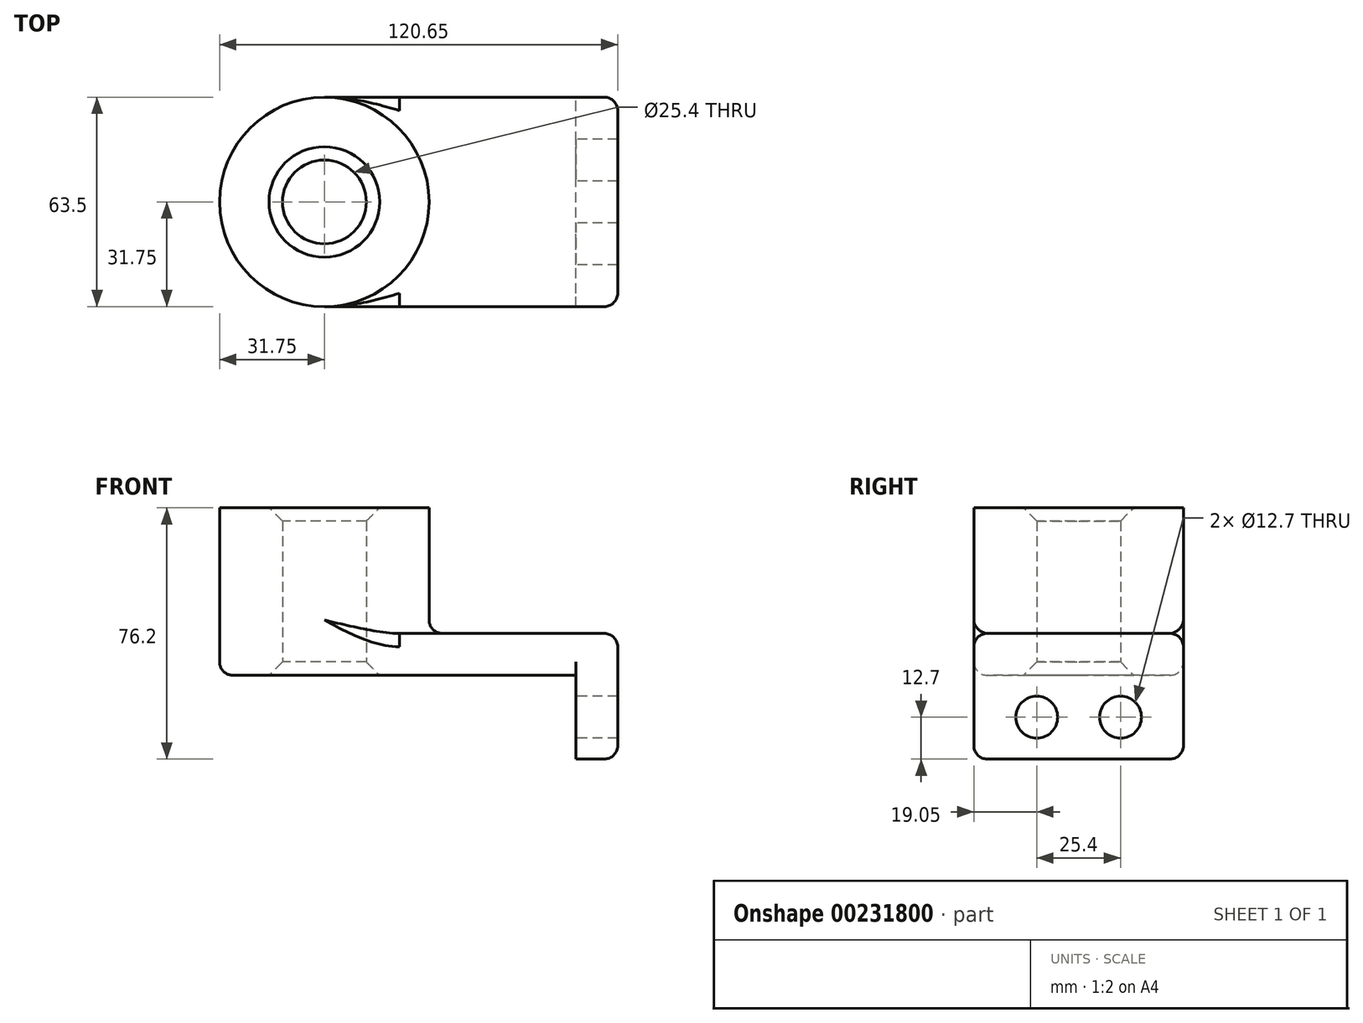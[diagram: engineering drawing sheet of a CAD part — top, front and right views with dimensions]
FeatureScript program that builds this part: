
annotation { "Feature Type Name" : "Feature", "Feature Type Description" : "" }
export const myFeature = defineFeature(function(context is Context, id is Id, definition is map)
    precondition{}
    {
        {
            var Q0;
            Q0=qCreatedBy(makeId("Top.planeOp"),FACE);
            var sketch = newSketch(context, id + "F0", { "sketchPlane" : qUnion([Q0])});
            skLineSegment(sketch, "E0.bottom", {"start": v(-38.1, -31.75) * mm, "end": v(38.1, -31.75) * mm});
            skLineSegment(sketch, "E0.top", {"start": v(-38.1, 31.75) * mm, "end": v(38.1, 31.75) * mm});
            skLineSegment(sketch, "E0.left", {"start": v(-38.1, -31.75) * mm, "end": v(-38.1, 31.75) * mm});
            skLineSegment(sketch, "E0.right", {"start": v(38.1, -31.75) * mm, "end": v(38.1, 31.75) * mm});
            skPoint(sketch, "E0.middle", {"position": v(0, 0) * mm});
            skCircle(sketch, "E1", {"center": v(-38.1, 0) * mm, "radius": 31.75 * mm});
            skCircle(sketch, "E2", {"center": v(-38.1, 0) * mm, "radius": 12.7 * mm});
            skSolve(sketch);
        }
        {
            var Q0;
            Q0 = qSketchRegion(id + "F0", true);
            extrude(context, id + "F1", {"entities" : qUnion([Q0]), "depth" : 12.7 * mm});
        }
        {
            var Q0;
            {var subQ1=sQuery(id+"F0.wireOp",EDGE,"E0.left");var subQ3=sQuery(id+"F0.wireOp",EDGE,"E2");var subQ4=makeQuery(id+"F0.imprint","INTERSECT",VERTEX,{"disambiguationData":[OD(0.0)],"derivedFrom":[subQ1,subQ3]});Q0=makeQuery(id+"F0.imprint","IMPRINT",FACE,{"disambiguationData":[TD([[makeQuery(id+"F0.imprint","IMPRINT",EDGE,{"disambiguationData":[TD([[subQ4,1.0]])],"derivedFrom":subQ3}),-1.0]])]});}
            var Q1;
            {var subQ1=sQuery(id+"F0.wireOp",EDGE,"E0.left");var subQ3=sQuery(id+"F0.wireOp",EDGE,"E2");var subQ4=makeQuery(id+"F0.imprint","INTERSECT",VERTEX,{"disambiguationData":[OD(0.0)],"derivedFrom":[subQ1,subQ3]});Q1=makeQuery(id+"F0.imprint","IMPRINT",FACE,{"disambiguationData":[TD([[makeQuery(id+"F0.imprint","IMPRINT",EDGE,{"disambiguationData":[TD([[subQ4,-1.0]])],"derivedFrom":subQ3}),-1.0]])]});}
            extrude(context, id + "F2", {"entities" : qUnion([Q0, Q1]), "operationType" : NewBodyOperationType.ADD, "depth" : 50.8 * mm});
        }
        {
            var Q0;
            Q0=makeQuery(id+"F1.opExtrude","SWEPT_FACE",FACE,{"disambiguationData":[OSD([sQuery(id+"F0.wireOp",EDGE,"E0.right")])]});
            var sketch = newSketch(context, id + "F3", { "sketchPlane" : qUnion([Q0])});
            skLineSegment(sketch, "E3.bottom", {"start": v(-31.75, 12.7) * mm, "end": v(31.75, 12.7) * mm});
            skLineSegment(sketch, "E3.top", {"start": v(-31.75, -25.4) * mm, "end": v(31.75, -25.4) * mm});
            skLineSegment(sketch, "E3.left", {"start": v(-31.75, 12.7) * mm, "end": v(-31.75, -25.4) * mm});
            skLineSegment(sketch, "E3.right", {"start": v(31.75, 12.7) * mm, "end": v(31.75, -25.4) * mm});
            skCircle(sketch, "E4", {"center": v(-12.7, -12.7) * mm, "radius": 6.35 * mm});
            skLineSegment(sketch, "E5", {"start": v(0, 0) * mm, "end": v(0, -25.4) * mm});
            skCircle(sketch, "E6.MirrorC", {"center": v(12.7, -12.7) * mm, "radius": 6.35 * mm});
            skSolve(sketch);
        }
        {
            var Q0;
            Q0 = qSketchRegion(id + "F3", true);
            extrude(context, id + "F4", {"entities" : qUnion([Q0]), "operationType" : NewBodyOperationType.ADD, "depth" : 12.7 * mm});
        }
        {
            var Q0;
            {var subQ0=sQuery(id+"F0.wireOp",EDGE,"E1");Q0=makeQuery(id+"F2.boolean.opBoolean","INTERSECT",EDGE,{"derivedFrom":[makeQuery(id+"F1.opExtrude","CAP_FACE",FACE,{"disambiguationData":[OSD([sQuery(id+"F0.wireOp",EDGE,"E0.bottom"),sQuery(id+"F0.wireOp",EDGE,"E0.top"),sQuery(id+"F0.wireOp",EDGE,"E0.right"),subQ0,sQuery(id+"F0.wireOp",EDGE,"E2")])],"isStart":false}),makeQuery(id+"F2.opExtrude","SWEPT_FACE",FACE,{"disambiguationData":[OSD([subQ0])]})]});}
            var Q1;
            Q1=makeQuery(id+"F4.opExtrude","SWEPT_EDGE",EDGE,{"disambiguationData":[OSD([sQuery(id+"F3.wireOp",EDGE,"E3.top"),sQuery(id+"F3.wireOp",EDGE,"E3.right")])]});
            var Q2;
            Q2=makeQuery(id+"F4.opExtrude","SWEPT_EDGE",EDGE,{"disambiguationData":[OSD([sQuery(id+"F3.wireOp",EDGE,"E3.top"),sQuery(id+"F3.wireOp",EDGE,"E3.left")])]});
            var Q3;
            Q3=makeQuery(id+"F4.opExtrude","CAP_EDGE",EDGE,{"disambiguationData":[OSD([sQuery(id+"F3.wireOp",EDGE,"E3.bottom")])],"isStart":false});
            fillet(context, id + "F5", {"entities" : qUnion([Q0, Q1, Q2, Q3]), "radius" : 4.06 * mm, "tangentPropagation" : true, "allowEdgeOverflow" : false});
        }
        {
            var Q0;
            Q0=makeQuery(id+"F4.boolean.opBoolean","MERGE",EDGE,{"derivedFrom":[makeQuery(id+"F1.opExtrude","CAP_EDGE",EDGE,{"disambiguationData":[OSD([sQuery(id+"F0.wireOp",EDGE,"E0.top")])],"isStart":false}),makeQuery(id+"F4.opExtrude","SWEPT_EDGE",EDGE,{"disambiguationData":[OSD([sQuery(id+"F3.wireOp",EDGE,"E3.bottom"),sQuery(id+"F3.wireOp",EDGE,"E3.right")])]})]});
            var Q1;
            Q1=makeQuery(id+"F4.boolean.opBoolean","MERGE",EDGE,{"derivedFrom":[makeQuery(id+"F1.opExtrude","CAP_EDGE",EDGE,{"disambiguationData":[OSD([sQuery(id+"F0.wireOp",EDGE,"E0.bottom")])],"isStart":false}),makeQuery(id+"F4.opExtrude","SWEPT_EDGE",EDGE,{"disambiguationData":[OSD([sQuery(id+"F3.wireOp",EDGE,"E3.bottom"),sQuery(id+"F3.wireOp",EDGE,"E3.left")])]})]});
            var Q2;
            Q2=makeQuery(id+"F1.opExtrude","CAP_EDGE",EDGE,{"disambiguationData":[OSD([sQuery(id+"F0.wireOp",EDGE,"E0.bottom")])],"isStart":true});
            var Q3;
            Q3=makeQuery(id+"F1.opExtrude","CAP_EDGE",EDGE,{"disambiguationData":[OSD([sQuery(id+"F0.wireOp",EDGE,"E0.top")])],"isStart":true});
            var Q4;
            Q4=makeQuery(id+"F1.opExtrude","CAP_EDGE",EDGE,{"disambiguationData":[OSD([sQuery(id+"F0.wireOp",EDGE,"E0.right")])],"isStart":true});
            fillet(context, id + "F6", {"entities" : qUnion([Q0, Q1, Q2, Q3, Q4]), "radius" : 4.06 * mm, "tangentPropagation" : true, "allowEdgeOverflow" : false});
        }
        {
            var Q0;
            {var subQ0=sQuery(id+"F0.wireOp",EDGE,"E2");Q0=makeQuery(id+"F2.boolean.opBoolean","MERGE",FACE,{"derivedFrom":[makeQuery(id+"F1.opExtrude","SWEPT_FACE",FACE,{"disambiguationData":[OSD([subQ0])]}),makeQuery(id+"F2.opExtrude","SWEPT_FACE",FACE,{"disambiguationData":[OSD([subQ0])]})]});}
            chamfer(context, id + "F7", {"entities" : qUnion([Q0]), "width" : 4.06 * mm, "tangentPropagation" : true});
        }
    });
